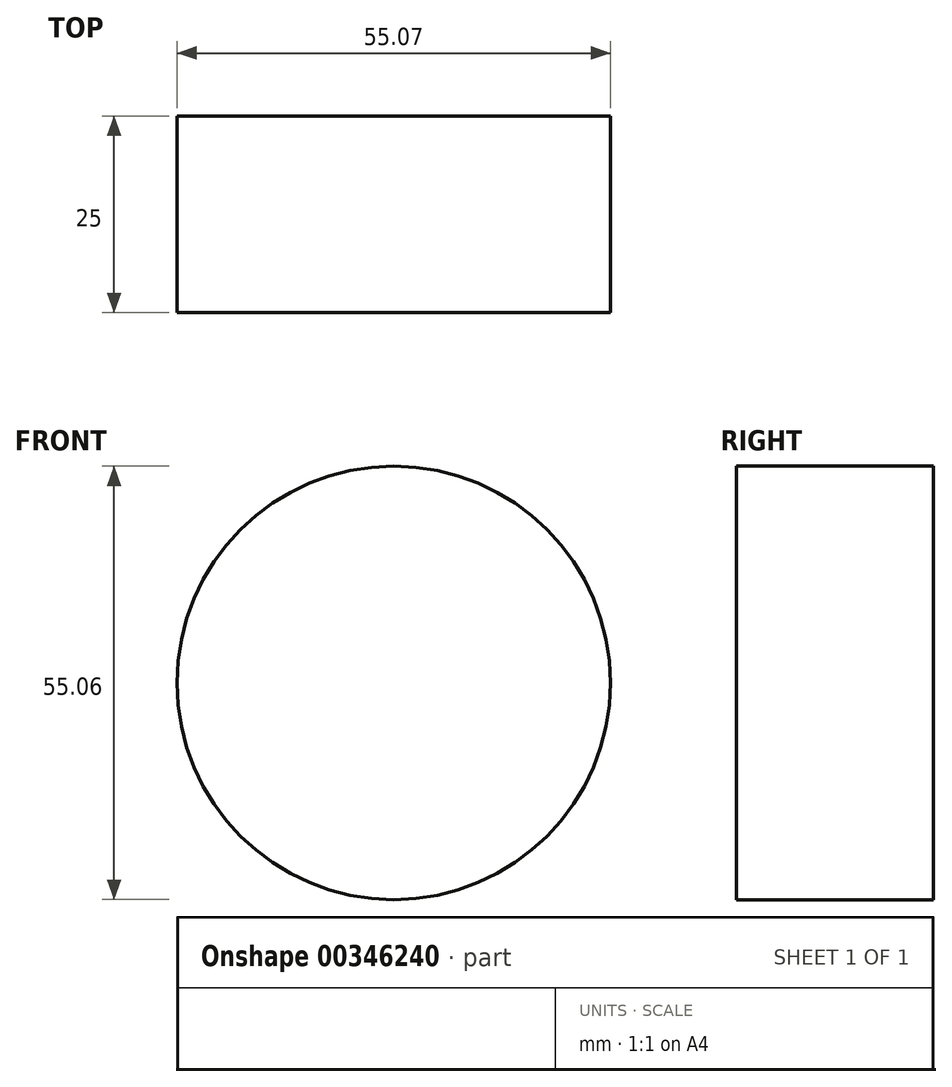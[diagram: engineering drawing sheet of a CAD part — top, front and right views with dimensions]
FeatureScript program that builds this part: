
annotation { "Feature Type Name" : "Feature", "Feature Type Description" : "" }
export const myFeature = defineFeature(function(context is Context, id is Id, definition is map)
    precondition{}
    {
        {
            var Q0;
            Q0=qCreatedBy(makeId("Front.planeOp"),FACE);
            var sketch = newSketch(context, id + "F0", { "sketchPlane" : qUnion([Q0])});
            skCircle(sketch, "E0", {"center": v(-12.9, 24.32) * mm, "radius": 27.53 * mm});
            skPoint(sketch, "E0.first.point", {"position": v(0, 0) * mm});
            skPoint(sketch, "E0.second.point", {"position": v(-33.48, 42.62) * mm});
            skPoint(sketch, "E0.third.point", {"position": v(13.48, 32.18) * mm});
            skSolve(sketch);
        }
        {
            var Q0;
            Q0=makeQuery(id+"F0.imprint","IMPRINT",FACE,{"disambiguationData":[TD([[makeQuery(id+"F0.imprint","IMPRINT",EDGE,{"derivedFrom":sQuery(id+"F0.wireOp",EDGE,"E0")}),1.0]])]});
            extrude(context, id + "F1", {"entities" : qUnion([Q0]), "depth" : 25 * mm});
        }
    });
